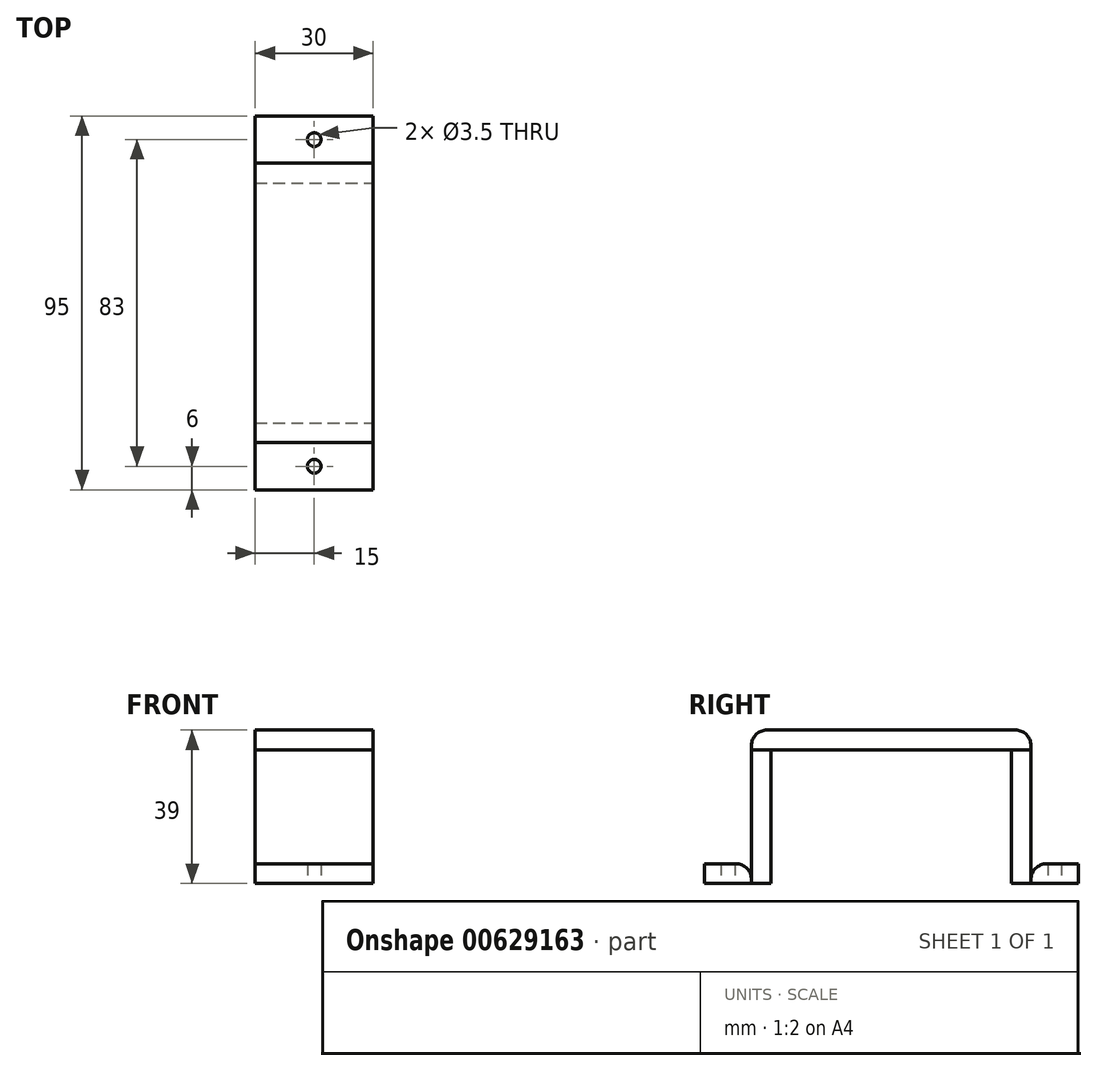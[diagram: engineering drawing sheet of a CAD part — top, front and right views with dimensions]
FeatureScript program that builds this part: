
annotation { "Feature Type Name" : "Feature", "Feature Type Description" : "" }
export const myFeature = defineFeature(function(context is Context, id is Id, definition is map)
    precondition{}
    {
        {
            var Q0;
            Q0=qCreatedBy(makeId("Top.planeOp"),FACE);
            var sketch = newSketch(context, id + "F0", { "sketchPlane" : qUnion([Q0])});
            skLineSegment(sketch, "E0.bottom", {"start": v(0, 0) * mm, "end": v(30, 0) * mm});
            skLineSegment(sketch, "E0.top", {"start": v(0, 5) * mm, "end": v(30, 5) * mm});
            skLineSegment(sketch, "E0.left", {"start": v(0, 0) * mm, "end": v(0, 5) * mm});
            skLineSegment(sketch, "E0.right", {"start": v(30, 0) * mm, "end": v(30, 5) * mm});
            skLineSegment(sketch, "E1", {"start": v(0, 5) * mm, "end": v(0, 35.5) * mm, "construction": true});
            skLineSegment(sketch, "E2", {"start": v(0, 35.5) * mm, "end": v(13.48, 35.5) * mm, "construction": true});
            skLineSegment(sketch, "E3.MirrorCS", {"start": v(0, 66) * mm, "end": v(30, 66) * mm});
            skLineSegment(sketch, "E4.MirrorCS", {"start": v(0, 71) * mm, "end": v(0, 66) * mm});
            skLineSegment(sketch, "E5.MirrorCS", {"start": v(0, 71) * mm, "end": v(30, 71) * mm});
            skLineSegment(sketch, "E6.MirrorCS", {"start": v(30, 71) * mm, "end": v(30, 66) * mm});
            skLineSegment(sketch, "E7", {"start": v(0, 0) * mm, "end": v(0, -12) * mm});
            skLineSegment(sketch, "E8", {"start": v(0, -12) * mm, "end": v(30, -12) * mm});
            skLineSegment(sketch, "E9", {"start": v(30, -12) * mm, "end": v(30, 0) * mm});
            skLineSegment(sketch, "E10", {"start": v(15, 0) * mm, "end": v(15, -12) * mm, "construction": true});
            skCircle(sketch, "E11", {"center": v(15, -6) * mm, "radius": 1.75 * mm});
            skLineSegment(sketch, "E12.MirrorCS", {"start": v(0, 71) * mm, "end": v(0, 83) * mm});
            skCircle(sketch, "E13.MirrorC", {"center": v(15, 77) * mm, "radius": 1.75 * mm});
            skLineSegment(sketch, "E14.MirrorCS", {"start": v(0, 83) * mm, "end": v(30, 83) * mm});
            skLineSegment(sketch, "E15.MirrorCS", {"start": v(30, 83) * mm, "end": v(30, 71) * mm});
            skSolve(sketch);
        }
        {
            var Q0;
            Q0=makeQuery(id+"F0.imprint","IMPRINT",FACE,{"disambiguationData":[TD([[makeQuery(id+"F0.imprint","IMPRINT",EDGE,{"derivedFrom":sQuery(id+"F0.wireOp",EDGE,"E3.MirrorCS")}),1.0]])]});
            var Q1;
            Q1=makeQuery(id+"F0.imprint","IMPRINT",FACE,{"disambiguationData":[TD([[makeQuery(id+"F0.imprint","IMPRINT",EDGE,{"derivedFrom":sQuery(id+"F0.wireOp",EDGE,"E0.bottom")}),1.0]])]});
            extrude(context, id + "F1", {"entities" : qUnion([Q0, Q1]), "depth" : 34 * mm, "offsetDistance" : 25 * mm});
        }
        {
            var Q0;
            Q0=makeQuery(id+"F0.imprint","IMPRINT",FACE,{"disambiguationData":[TD([[makeQuery(id+"F0.imprint","IMPRINT",EDGE,{"derivedFrom":sQuery(id+"F0.wireOp",EDGE,"E5.MirrorCS")}),1.0]])]});
            var Q1;
            Q1=makeQuery(id+"F0.imprint","IMPRINT",FACE,{"disambiguationData":[TD([[makeQuery(id+"F0.imprint","IMPRINT",EDGE,{"derivedFrom":sQuery(id+"F0.wireOp",EDGE,"E0.bottom")}),-1.0]])]});
            extrude(context, id + "F2", {"entities" : qUnion([Q0, Q1]), "depth" : 5 * mm, "offsetDistance" : 25 * mm});
        }
        {
            var Q0;
            Q0=makeQuery(id+"F1.opExtrude","CAP_FACE",FACE,{"disambiguationData":[OSD([sQuery(id+"F0.wireOp",EDGE,"E3.MirrorCS"),sQuery(id+"F0.wireOp",EDGE,"E4.MirrorCS"),sQuery(id+"F0.wireOp",EDGE,"E5.MirrorCS"),sQuery(id+"F0.wireOp",EDGE,"E6.MirrorCS")])],"isStart":false});
            var sketch = newSketch(context, id + "F3", { "sketchPlane" : qUnion([Q0])});
            skPoint(sketch, "E16.0", {"position": v(30, 0) * mm});
            skLineSegment(sketch, "E17.bottom", {"start": v(0, 71) * mm, "end": v(30, 71) * mm});
            skLineSegment(sketch, "E17.top", {"start": v(0, 0) * mm, "end": v(30, 0) * mm});
            skLineSegment(sketch, "E17.left", {"start": v(0, 71) * mm, "end": v(0, 0) * mm});
            skLineSegment(sketch, "E17.right", {"start": v(30, 71) * mm, "end": v(30, 0) * mm});
            skSolve(sketch);
        }
        {
            var Q0;
            {var subQ0=sQuery(id+"F3.wireOp",EDGE,"E17.bottom");Q0=makeQuery(id+"F3.imprint","IMPRINT",FACE,{"disambiguationData":[TD([[makeQuery(id+"F3.imprint","IMPRINT",EDGE,{"derivedFrom":subQ0}),-1.0]])]});}
            var Q1;
            {var subQ0=sQuery(id+"F3.wireOp",EDGE,"E17.top");Q1=makeQuery(id+"F3.imprint","IMPRINT",FACE,{"disambiguationData":[TD([[makeQuery(id+"F3.imprint","IMPRINT",EDGE,{"derivedFrom":subQ0}),1.0]])]});}
            extrude(context, id + "F4", {"entities" : qUnion([Q0, Q1]), "depth" : 5 * mm, "offsetDistance" : 25 * mm});
        }
        {
            var Q0;
            Q0=makeQuery(id+"F2.opExtrude","CAP_EDGE",EDGE,{"disambiguationData":[OSD([sQuery(id+"F0.wireOp",EDGE,"E0.bottom")])],"isStart":false});
            var Q1;
            Q1=makeQuery(id+"F4.opExtrude","CAP_EDGE",EDGE,{"disambiguationData":[OSD([sQuery(id+"F3.wireOp",EDGE,"E17.top")])],"isStart":false});
            var Q2;
            Q2=makeQuery(id+"F4.opExtrude","CAP_EDGE",EDGE,{"disambiguationData":[OSD([sQuery(id+"F3.wireOp",EDGE,"E17.bottom")])],"isStart":false});
            var Q3;
            Q3=makeQuery(id+"F2.opExtrude","CAP_EDGE",EDGE,{"disambiguationData":[OSD([sQuery(id+"F0.wireOp",EDGE,"E5.MirrorCS")])],"isStart":false});
            fillet(context, id + "F5", {"entities" : qUnion([Q0, Q1, Q2, Q3]), "radius" : 4 * mm, "tangentPropagation" : true, "allowEdgeOverflow" : false});
        }
    });
